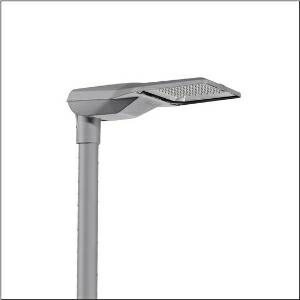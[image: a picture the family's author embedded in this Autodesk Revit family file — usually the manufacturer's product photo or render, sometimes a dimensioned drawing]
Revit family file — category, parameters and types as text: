
# Revit family: streetlight_sl_21_iq_midi___st0_8a_5xe3c31d08mb_7ea8
name_source: partatom
category: Lighting Fixtures
units: mm (PartAtom-declared; Revit-internal decimal feet)

## family parameters
Cut with Voids When Loaded = No
Host = Face
Light Source = No
Part Type = Normal
Room Calculation Point = No
Round Connector Dimension = Use Diameter
Shared = No

## types (1)
- --- (1 x LED, 19500 lm, 146.7 W, 3000K)
    Apparent Load = 147 VA
    CIE Flux Codes = 38 75 97 100 100
    Color Rendering = 70
    Color Temperature = 3000K
    Default Elevation = 1800 mm
    Description = Streetlight SL 21 iQ midi, mast luminaire, primary light control with lens, of PMMA, primary optical cover: cover, of toughened safety glass, transparent, light distribution: ST0.8a, light emission: direct distribution, primary light characteristic: asymmetric, installation type: post-top, side-entry, LED, High Power LED, rated luminous flux: 19.500lm, luminous efficacy: 133lm/W, light colour: 730, colour temperature: 3000K, control gear: iQ-Comfort, control: Auto-Match, Temp-Guard, Lumen-Switch, Night-Set, Smart-Wire, Light-Fading, Desk-Remote (wireless, voltage-free reading and setting of iQ features in the workshop via application-optimized NFC function/RFID function), optimised constant luminous flux control (CLO 2.0), pre-setting: linear dimming characteristic, mains connection: 230..240V, AC, 50/60Hz, start of lifetime: 147W, end of service life: 161W, reduction: 62W, luminaire housing, of diecast aluminium, powder-coated, Siteco® metallic grey (DB 702S), corrosivity category C5 mid according to DIN EN ISO 12944, please order mast flange separately, inclination adjustable: 0°, 5°, 10°, 15°, sealing non-destructively replaceable, multi-level sealing system, length: 644mm, width: 335mm, height: 110mm, mast flange for spigot size: 42mm (side-entry): 5XC10008XM4, 60/48mm (side-entry/post-top): 5XC10108XM2, 76/60mm (side-entry/post-top): 5XC10108XM1, mounting height: 4..8m, protection rating (complete): IP66, insulation class (complete): insulation class II (safety insulation), certification: CE, ENEC, ENEC+, VDE, impact resistance: IK10, permissible operating ambient temperature for outdoor applications: -40..+50°C, standard-compliant lighting for roads and squares, packaging unit: 1 piece

Light Distribution: ST0.8a
    Height = 111 mm
    Lamp = 1 x LED
    Lamp Light Flux = 19500 lm
    Lamp Power = 146.7 W
    Lamp count = 1
    Length = 644 mm
    Luminous efficacy = 133 lm/W
    Manufacturer = Siteco
    ModVariant = No
    Model = 5XE3C31D08MB
    Number of Poles = 1
    OnlyDefault = Yes
    Power Factor = 1
    Product Name = Streetlight SL 21 iQ midi | ST0.8a
    Product group = mast luminaire | pylon top
    ProductGroupID = 6100
    Protection Class = Protection class II
    Protection Degree = IP 66
    RLX_Detail_Level = 1
    RLX_Emergency_Light_Flux = 0 lm
    RLX_Emergency_Type = 0
    RLX_Emergency_Type_DB = No
    RlxData = <blob elided: 27037 chars, md5=e345e632>
    Socket = socket
    Standby Power = 0 W
    System Light Flux = 19499 lm
    System Power = 147 W
    Type Comments = factory setting: luminous flux: 100 % | dim-lin: 254 | 753 mA
    Type Image = l_1004298.jpg
    URL = http://relux.com
    VarID = @adj_207557
    Voltage = 0 V
    Weight = 0.00 kg
    Width = 336 mm

## geometry (parser evidence)
native form markers: Blend x4, Sweep x11
no freeform markers — native parametric forms only
